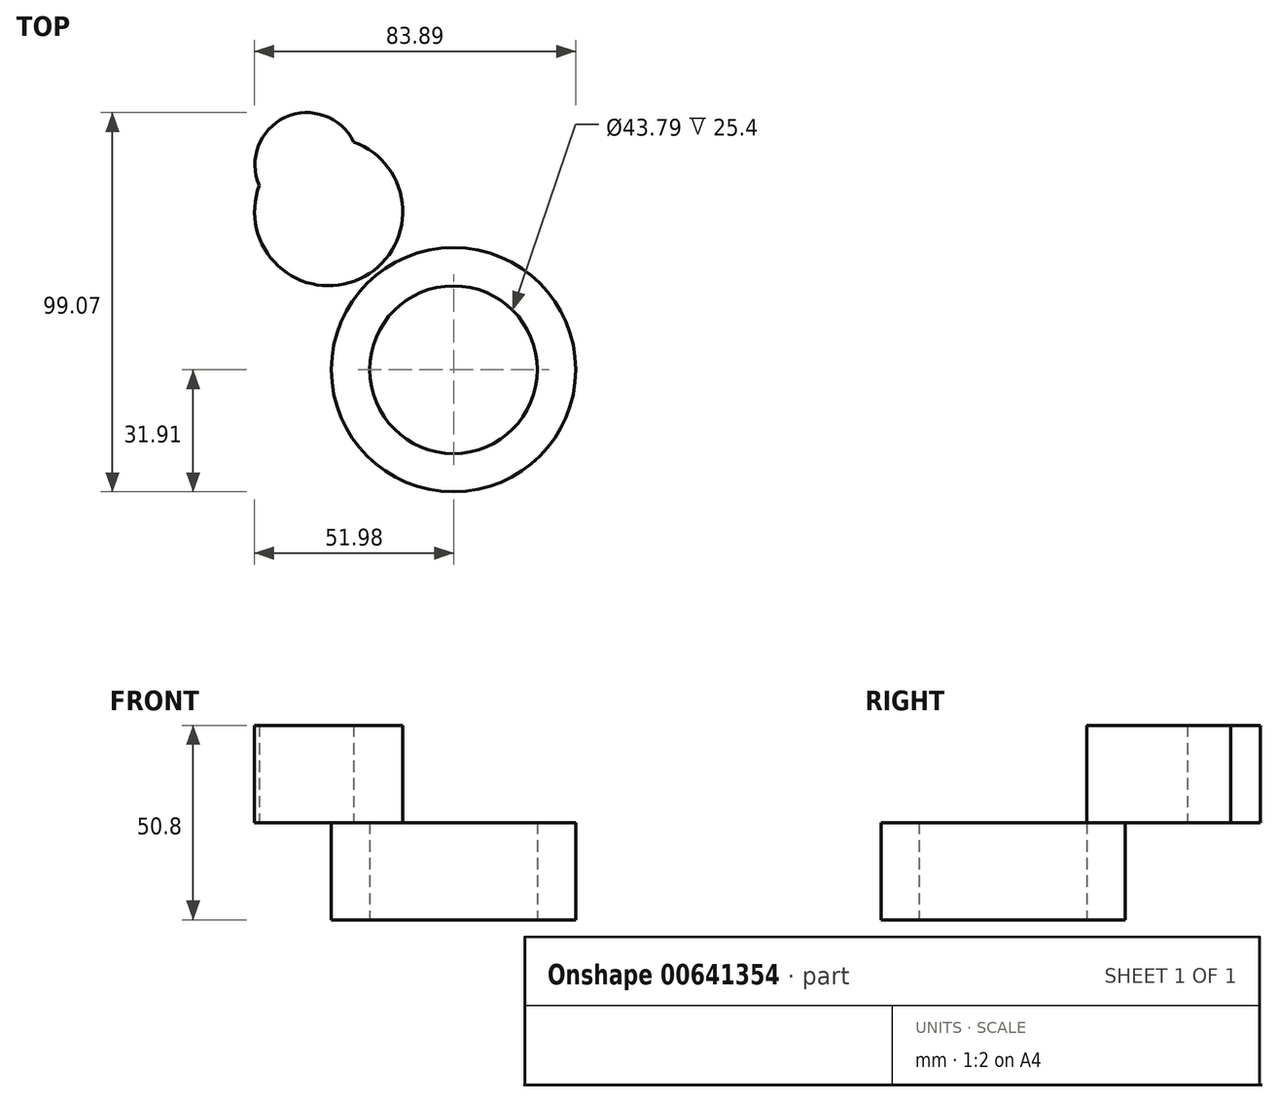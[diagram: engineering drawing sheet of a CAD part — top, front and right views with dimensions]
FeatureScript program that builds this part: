
annotation { "Feature Type Name" : "Feature", "Feature Type Description" : "" }
export const myFeature = defineFeature(function(context is Context, id is Id, definition is map)
    precondition{}
    {
        {
            var Q0;
            Q0=qCreatedBy(makeId("Top.planeOp"),FACE);
            var sketch = newSketch(context, id + "F0", { "sketchPlane" : qUnion([Q0])});
            skCircle(sketch, "E0", {"center": v(0, 0) * mm, "radius": 31.9 * mm});
            skCircle(sketch, "E1", {"center": v(0, 0) * mm, "radius": 21.9 * mm});
            skCircle(sketch, "E2", {"center": v(0, 0) * mm, "radius": 12.79 * mm});
            skCircle(sketch, "E3", {"center": v(0, 0) * mm, "radius": 4.66 * mm});
            skSolve(sketch);
        }
        {
            var Q0;
            Q0 = qSketchRegion(id + "F0", true);
            extrude(context, id + "F1", {"entities" : qUnion([Q0]), "depth" : 25.4 * mm, "offsetDistance" : 25.4 * mm});
        }
        {
            var Q0;
            Q0=makeQuery(id+"F1.opExtrude","CAP_FACE",FACE,{"disambiguationData":[OSD([sQuery(id+"F0.wireOp",EDGE,"E0"),sQuery(id+"F0.wireOp",EDGE,"E1")])],"isStart":false});
            var sketch = newSketch(context, id + "F2", { "sketchPlane" : qUnion([Q0])});
            skCircle(sketch, "E4", {"center": v(-32.62, 41.28) * mm, "radius": 19.36 * mm});
            skPoint(sketch, "E4.first.point", {"position": v(-49.87, 50.05) * mm});
            skPoint(sketch, "E4.second.point", {"position": v(-27.3, 22.67) * mm});
            skPoint(sketch, "E4.third.point", {"position": v(-15.02, 49.34) * mm});
            skCircle(sketch, "E5", {"center": v(-38.3, 53.6) * mm, "radius": 13.57 * mm});
            skPoint(sketch, "E5.second.point", {"position": v(-50.72, 48.12) * mm});
            skPoint(sketch, "E5.third.point", {"position": v(-28.54, 44.18) * mm});
            skSolve(sketch);
        }
        {
            var Q0;
            Q0 = qSketchRegion(id + "F2", true);
            extrude(context, id + "F3", {"entities" : qUnion([Q0]), "depth" : 25.4 * mm, "offsetDistance" : 25.4 * mm});
        }
    });
